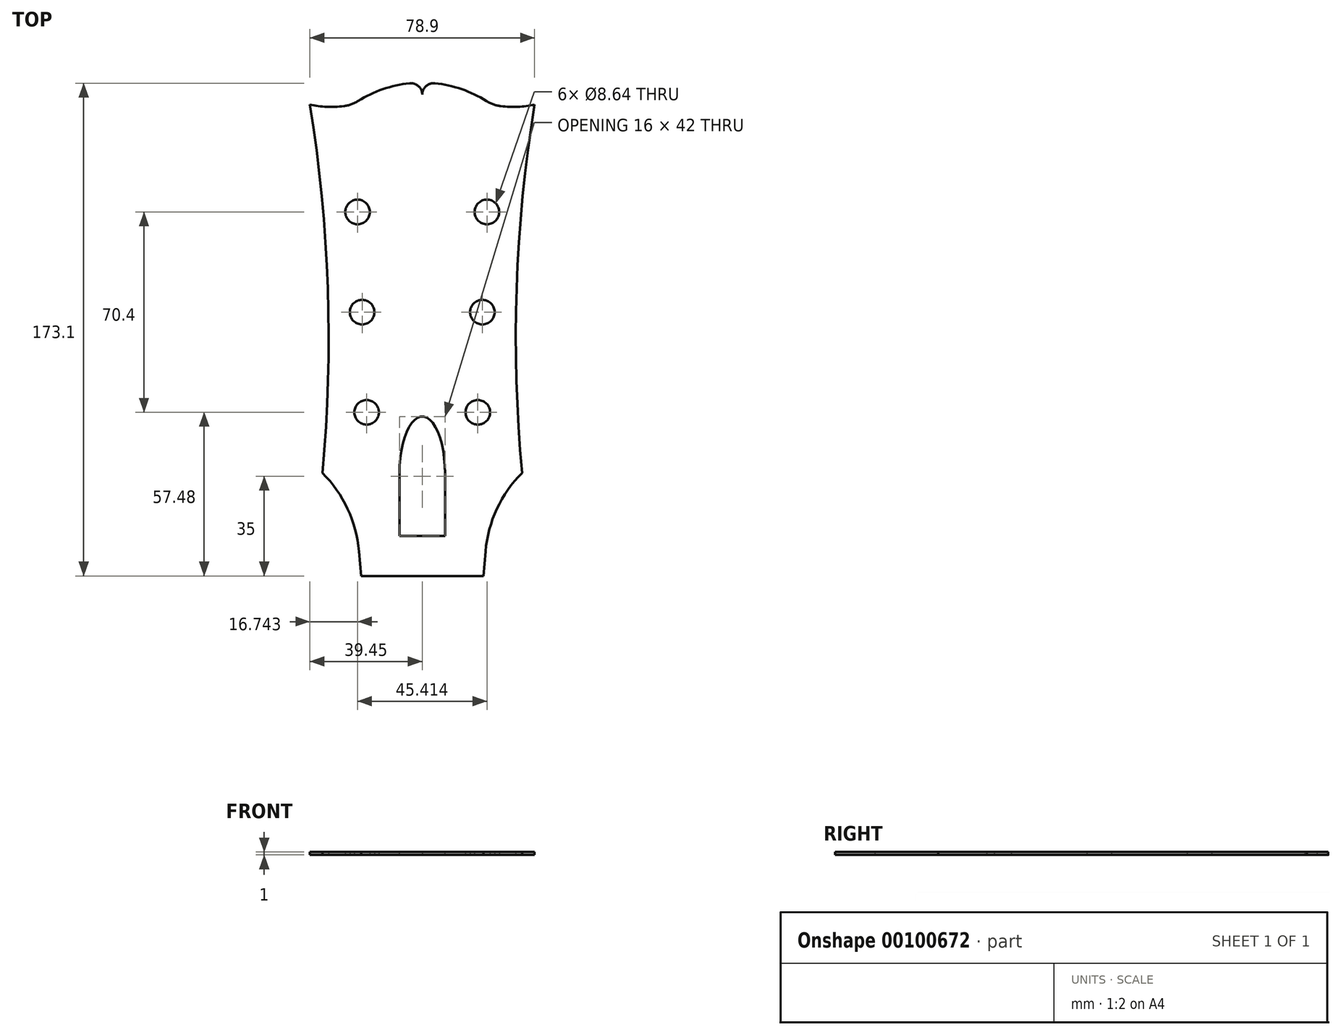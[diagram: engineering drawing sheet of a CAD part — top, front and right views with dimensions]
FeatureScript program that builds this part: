
annotation { "Feature Type Name" : "Feature", "Feature Type Description" : "" }
export const myFeature = defineFeature(function(context is Context, id is Id, definition is map)
    precondition{}
    {
        {
            var Q0;
            Q0=qCreatedBy(makeId("Top.planeOp"),FACE);
            var sketch = newSketch(context, id + "F0", { "sketchPlane" : qUnion([Q0])});
            skPoint(sketch, "E0.middle", {"position": v(0, 0) * mm});
            skLineSegment(sketch, "E1", {"start": v(0, 0) * mm, "end": v(0, 36.2) * mm, "construction": true});
            skLineSegment(sketch, "E2", {"start": v(0, 36.2) * mm, "end": v(0, 57.48) * mm, "construction": true});
            skLineSegment(sketch, "E3", {"start": v(0, 57.48) * mm, "end": v(0, 92.68) * mm, "construction": true});
            skLineSegment(sketch, "E4", {"start": v(0, 92.68) * mm, "end": v(0, 127.88) * mm, "construction": true});
            skLineSegment(sketch, "E5", {"start": v(0, 0) * mm, "end": v(-21.45, 0) * mm});
            skLineSegment(sketch, "E6", {"start": v(0, 36.2) * mm, "end": v(-35.05, 36.2) * mm, "construction": true});
            skLineSegment(sketch, "E7", {"start": v(0, 127.88) * mm, "end": v(0, 165.6) * mm, "construction": true});
            skLineSegment(sketch, "E8", {"start": v(0, 165.6) * mm, "end": v(-39.45, 165.6) * mm, "construction": true});
            skLineSegment(sketch, "E9", {"start": v(0, 92.68) * mm, "end": v(-32.93, 92.68) * mm, "construction": true});
            skArc(sketch, "E10", {"start": v(-35.05, 36.2) * mm, "mid": v(-33.15, 101.04) * mm, "end": v(-39.45, 165.6) * mm});
            skLineSegment(sketch, "E11", {"start": v(0, 165.6) * mm, "end": v(0, 173.31) * mm, "construction": true});
            skLineSegment(sketch, "E12", {"start": v(-21.45, 0) * mm, "end": v(-22.2, 8.66) * mm});
            skLineSegment(sketch, "E13", {"start": v(-35.05, 36.2) * mm, "end": v(-23.62, 24.77) * mm, "construction": true});
            skArc(sketch, "E14", {"start": v(-22.2, 8.66) * mm, "mid": v(-26.2, 23.56) * mm, "end": v(-35.05, 36.2) * mm});
            skArc(sketch, "E15", {"start": v(-4.44, 173.08) * mm, "mid": v(-13.83, 171) * mm, "end": v(-22.52, 166.86) * mm});
            skArc(sketch, "E16", {"start": v(-39.45, 165.6) * mm, "mid": v(-33.54, 164.82) * mm, "end": v(-27.59, 165.05) * mm});
            skArc(sketch, "E17", {"start": v(0, 169.08) * mm, "mid": v(-1.33, 172.07) * mm, "end": v(-4.44, 173.08) * mm});
            skArc(sketch, "E18.MirrorCS", {"start": v(39.45, 165.6) * mm, "mid": v(33.54, 164.82) * mm, "end": v(27.59, 165.05) * mm});
            skArc(sketch, "E19.MirrorCS", {"start": v(22.2, 8.66) * mm, "mid": v(26.2, 23.56) * mm, "end": v(35.05, 36.2) * mm});
            skArc(sketch, "E20.MirrorCS", {"start": v(35.05, 36.2) * mm, "mid": v(33.15, 101.04) * mm, "end": v(39.45, 165.6) * mm});
            skLineSegment(sketch, "E21.MirrorCS", {"start": v(35.05, 36.2) * mm, "end": v(23.62, 24.77) * mm, "construction": true});
            skLineSegment(sketch, "E22.MirrorCS", {"start": v(21.45, 0) * mm, "end": v(22.2, 8.66) * mm});
            skArc(sketch, "E23.MirrorCS", {"start": v(4.44, 173.08) * mm, "mid": v(13.83, 171) * mm, "end": v(22.52, 166.86) * mm});
            skLineSegment(sketch, "E24.MirrorCS", {"start": v(0, 0) * mm, "end": v(21.45, 0) * mm});
            skArc(sketch, "E25.MirrorCS", {"start": v(0, 169.08) * mm, "mid": v(1.33, 172.07) * mm, "end": v(4.44, 173.08) * mm});
            skArc(sketch, "E26", {"start": v(22.52, 166.86) * mm, "mid": v(24.95, 165.68) * mm, "end": v(27.59, 165.05) * mm});
            skLineSegment(sketch, "E27.direction1", {"start": v(0, 0) * mm, "end": v(50, 0) * mm, "construction": true});
            skArc(sketch, "E28.MirrorC", {"start": v(-22.52, 166.86) * mm, "mid": v(-24.95, 165.68) * mm, "end": v(-27.59, 165.05) * mm});
            skPoint(sketch, "E29.orphan", {"position": v(24.41, 165.6) * mm});
            skPoint(sketch, "E30.orphan", {"position": v(-24.41, 165.6) * mm});
            skSolve(sketch);
        }
        {
            var Q0;
            Q0 = qSketchRegion(id + "F0", true);
            extrude(context, id + "F1", {"entities" : qUnion([Q0]), "depth" : 1 * mm});
        }
        {
            var Q0;
            Q0=makeQuery(id+"F1.opExtrude","CAP_FACE",FACE,{"disambiguationData":[OSD([sQuery(id+"F0.wireOp",EDGE,"E5"),sQuery(id+"F0.wireOp",EDGE,"E10"),sQuery(id+"F0.wireOp",EDGE,"E12"),sQuery(id+"F0.wireOp",EDGE,"E14"),sQuery(id+"F0.wireOp",EDGE,"E15"),sQuery(id+"F0.wireOp",EDGE,"E16"),sQuery(id+"F0.wireOp",EDGE,"E17"),sQuery(id+"F0.wireOp",EDGE,"E18.MirrorCS"),sQuery(id+"F0.wireOp",EDGE,"E19.MirrorCS"),sQuery(id+"F0.wireOp",EDGE,"E20.MirrorCS"),sQuery(id+"F0.wireOp",EDGE,"E22.MirrorCS"),sQuery(id+"F0.wireOp",EDGE,"E23.MirrorCS"),sQuery(id+"F0.wireOp",EDGE,"E24.MirrorCS"),sQuery(id+"F0.wireOp",EDGE,"E25.MirrorCS")])],"isStart":false});
            var sketch = newSketch(context, id + "F2", { "sketchPlane" : qUnion([Q0])});
            skPoint(sketch, "E31", {"position": v(-22.7, 127.88) * mm});
            skPoint(sketch, "E32", {"position": v(-21.1, 92.68) * mm});
            skPoint(sketch, "E33", {"position": v(-19.51, 57.48) * mm});
            skPoint(sketch, "E34.MirrorP", {"position": v(19.51, 57.48) * mm});
            skPoint(sketch, "E35.MirrorP", {"position": v(21.1, 92.68) * mm});
            skPoint(sketch, "E36.MirrorP", {"position": v(22.7, 127.88) * mm});
            skLineSegment(sketch, "E37", {"start": v(19.5, 57.48) * mm, "end": v(22.84, 130.7) * mm, "construction": true});
            skLineSegment(sketch, "E38", {"start": v(0, 0) * mm, "end": v(0, 169.08) * mm, "construction": true});
            skLineSegment(sketch, "E39.MirrorCS", {"start": v(-19.5, 57.48) * mm, "end": v(-22.84, 130.7) * mm, "construction": true});
            skSolve(sketch);
        }
        {
            var Q0;
            Q0=sQuery(id+"F2.wireOp",VERTEX,"E33");
            var Q1;
            Q1=sQuery(id+"F2.wireOp",VERTEX,"E32");
            var Q2;
            Q2=sQuery(id+"F2.wireOp",VERTEX,"E31");
            var Q3;
            Q3=sQuery(id+"F2.wireOp",VERTEX,"E36.MirrorP");
            var Q4;
            Q4=sQuery(id+"F2.wireOp",VERTEX,"E35.MirrorP");
            var Q5;
            Q5=sQuery(id+"F2.wireOp",VERTEX,"E34.MirrorP");
            var Q6;
            Q6=makeQuery(id+"F1.opExtrude","SWEPT_BODY",BODY,{"disambiguationData":[OSD([sQuery(id+"F0.wireOp",EDGE,"E5"),sQuery(id+"F0.wireOp",EDGE,"E10"),sQuery(id+"F0.wireOp",EDGE,"E12"),sQuery(id+"F0.wireOp",EDGE,"E14"),sQuery(id+"F0.wireOp",EDGE,"E15"),sQuery(id+"F0.wireOp",EDGE,"E16"),sQuery(id+"F0.wireOp",EDGE,"E17"),sQuery(id+"F0.wireOp",EDGE,"E18.MirrorCS"),sQuery(id+"F0.wireOp",EDGE,"E19.MirrorCS"),sQuery(id+"F0.wireOp",EDGE,"E20.MirrorCS"),sQuery(id+"F0.wireOp",EDGE,"E22.MirrorCS"),sQuery(id+"F0.wireOp",EDGE,"E23.MirrorCS"),sQuery(id+"F0.wireOp",EDGE,"E24.MirrorCS"),sQuery(id+"F0.wireOp",EDGE,"E25.MirrorCS")])]});
            hole(context, id + "F3", {"style" : HoleStyle.SIMPLE, "endStyle" : HoleEndStyle.THROUGH, "holeDiameter" : 8.64 * mm, "locations" : qUnion([Q0, Q1, Q2, Q3, Q4, Q5]), "scope" : qUnion([Q6]), "isTappedThrough" : true, "startStyle" : HoleStartStyle.PART});
        }
        {
            var Q0;
            Q0=makeQuery(id+"F1.opExtrude","CAP_FACE",FACE,{"disambiguationData":[OSD([sQuery(id+"F0.wireOp",EDGE,"E5"),sQuery(id+"F0.wireOp",EDGE,"E10"),sQuery(id+"F0.wireOp",EDGE,"E12"),sQuery(id+"F0.wireOp",EDGE,"E14"),sQuery(id+"F0.wireOp",EDGE,"E15"),sQuery(id+"F0.wireOp",EDGE,"E16"),sQuery(id+"F0.wireOp",EDGE,"E17"),sQuery(id+"F0.wireOp",EDGE,"E18.MirrorCS"),sQuery(id+"F0.wireOp",EDGE,"E19.MirrorCS"),sQuery(id+"F0.wireOp",EDGE,"E20.MirrorCS"),sQuery(id+"F0.wireOp",EDGE,"E22.MirrorCS"),sQuery(id+"F0.wireOp",EDGE,"E23.MirrorCS"),sQuery(id+"F0.wireOp",EDGE,"E24.MirrorCS"),sQuery(id+"F0.wireOp",EDGE,"E25.MirrorCS"),sQuery(id+"F0.wireOp",EDGE,"E26"),sQuery(id+"F0.wireOp",EDGE,"E28.MirrorC")])],"isStart":false});
            var sketch = newSketch(context, id + "F5", { "sketchPlane" : qUnion([Q0])});
            skLineSegment(sketch, "E40", {"start": v(0, 0) * mm, "end": v(0, 14) * mm, "construction": true});
            skLineSegment(sketch, "E41", {"start": v(0, 14) * mm, "end": v(8, 14) * mm});
            skLineSegment(sketch, "E42", {"start": v(8, 14) * mm, "end": v(8, 36) * mm});
            skLineSegment(sketch, "E43", {"start": v(0, 14) * mm, "end": v(0, 36) * mm, "construction": true});
            skLineSegment(sketch, "E44", {"start": v(0, 36) * mm, "end": v(8, 36) * mm, "construction": true});
            skEllipticalArc(sketch, "E45", {});
            skLineSegment(sketch, "E46", {"start": v(0, 14) * mm, "end": v(0, 56) * mm, "construction": true});
            skLineSegment(sketch, "E47.MirrorCS", {"start": v(-8, 14) * mm, "end": v(-8, 36) * mm});
            skLineSegment(sketch, "E48.MirrorCS", {"start": v(0, 14) * mm, "end": v(-8, 14) * mm});
            const initialGuessFIZFSFSKmq9FpcvFH_1  = {"E45": [0, 0.036, 1, 0, 0.008, 0.02, 6.283185307179586, 3.141592653589793]};
            skSetInitialGuess(sketch, initialGuessFIZFSFSKmq9FpcvFH_1);
            skSolve(sketch);
        }
        {
            var Q0;
            Q0 = qSketchRegion(id + "F5", true);
            extrude(context, id + "F4", {"entities" : qUnion([Q0]), "operationType" : NewBodyOperationType.REMOVE, "oppositeDirection" : true, "depth" : 25 * mm});
        }
    });
